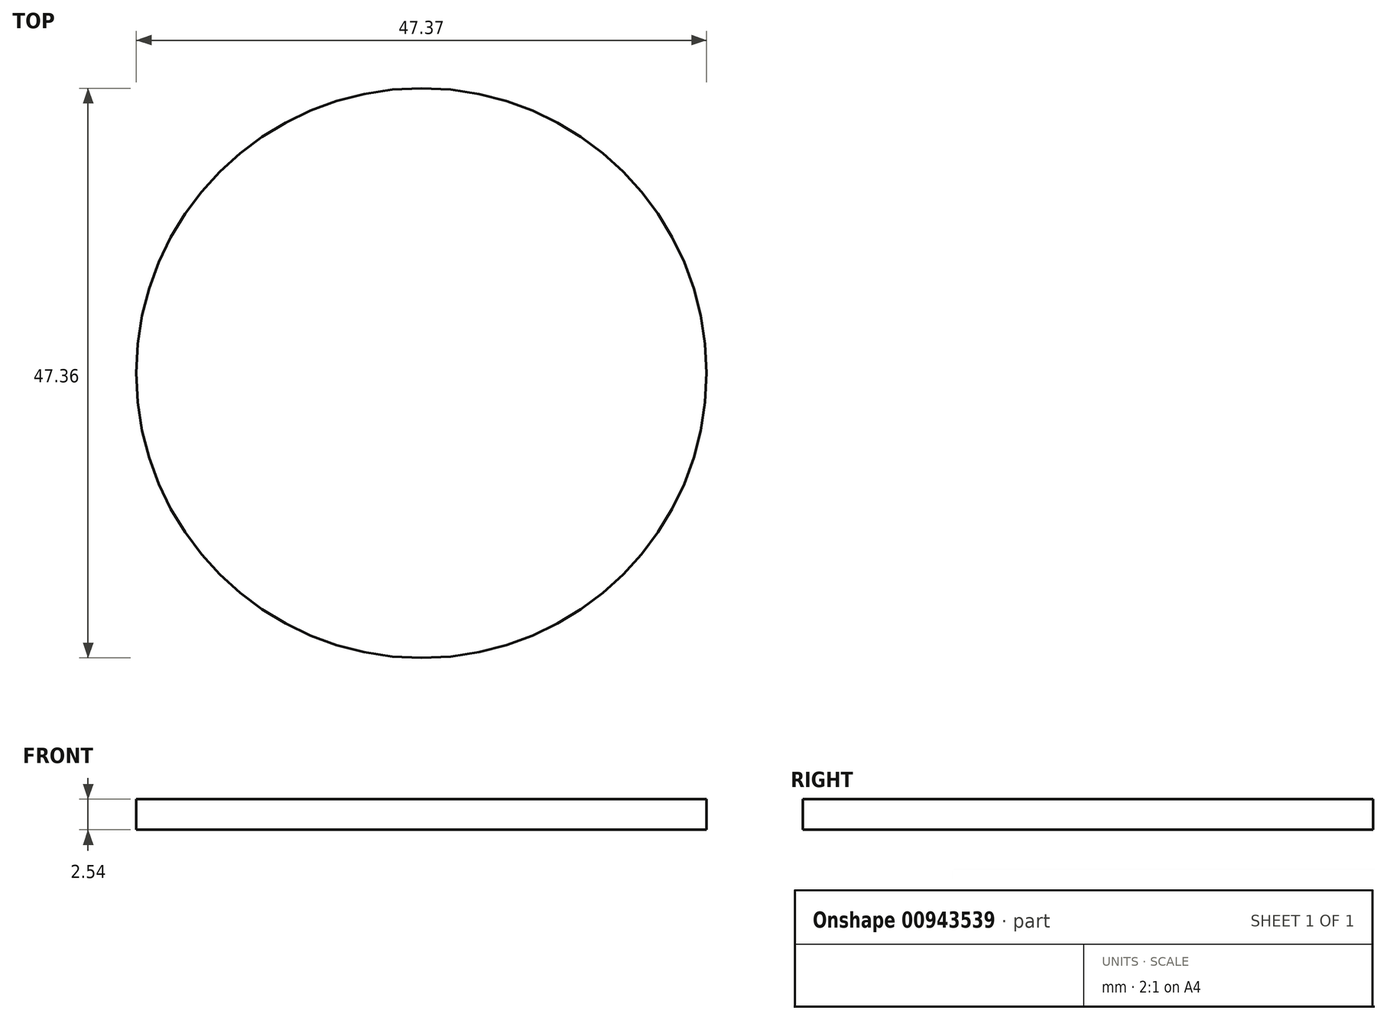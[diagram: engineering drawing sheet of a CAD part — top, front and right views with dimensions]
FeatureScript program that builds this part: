
annotation { "Feature Type Name" : "Feature", "Feature Type Description" : "" }
export const myFeature = defineFeature(function(context is Context, id is Id, definition is map)
    precondition{}
    {
        {
            var Q0;
            Q0=qCreatedBy(makeId("Top.planeOp"),FACE);
            var sketch = newSketch(context, id + "F0", { "sketchPlane" : qUnion([Q0])});
            skCircle(sketch, "E0", {"center": v(1.8, 0) * mm, "radius": 23.68 * mm});
            skSolve(sketch);
        }
        {
            var Q0;
            Q0 = qSketchRegion(id + "F0", true);
            extrude(context, id + "F1", {"entities" : qUnion([Q0]), "depth" : 25.4 * mm, "offsetDistance" : 25.4 * mm});
        }
        {
            var Q0;
            Q0=makeQuery(id+"F1.opExtrude","SWEPT_FACE",FACE,{"disambiguationData":[OSD([sQuery(id+"F0.wireOp",EDGE,"E0")])]});
            var Q1;
            Q1=makeQuery(id+"F1.opExtrude","CAP_FACE",FACE,{"disambiguationData":[OSD([sQuery(id+"F0.wireOp",EDGE,"E0")])],"isStart":true});
            shell(context, id + "F2", {"entities" : qUnion([Q0, Q1]), "thickness" : 2.54 * mm});
        }
    });
